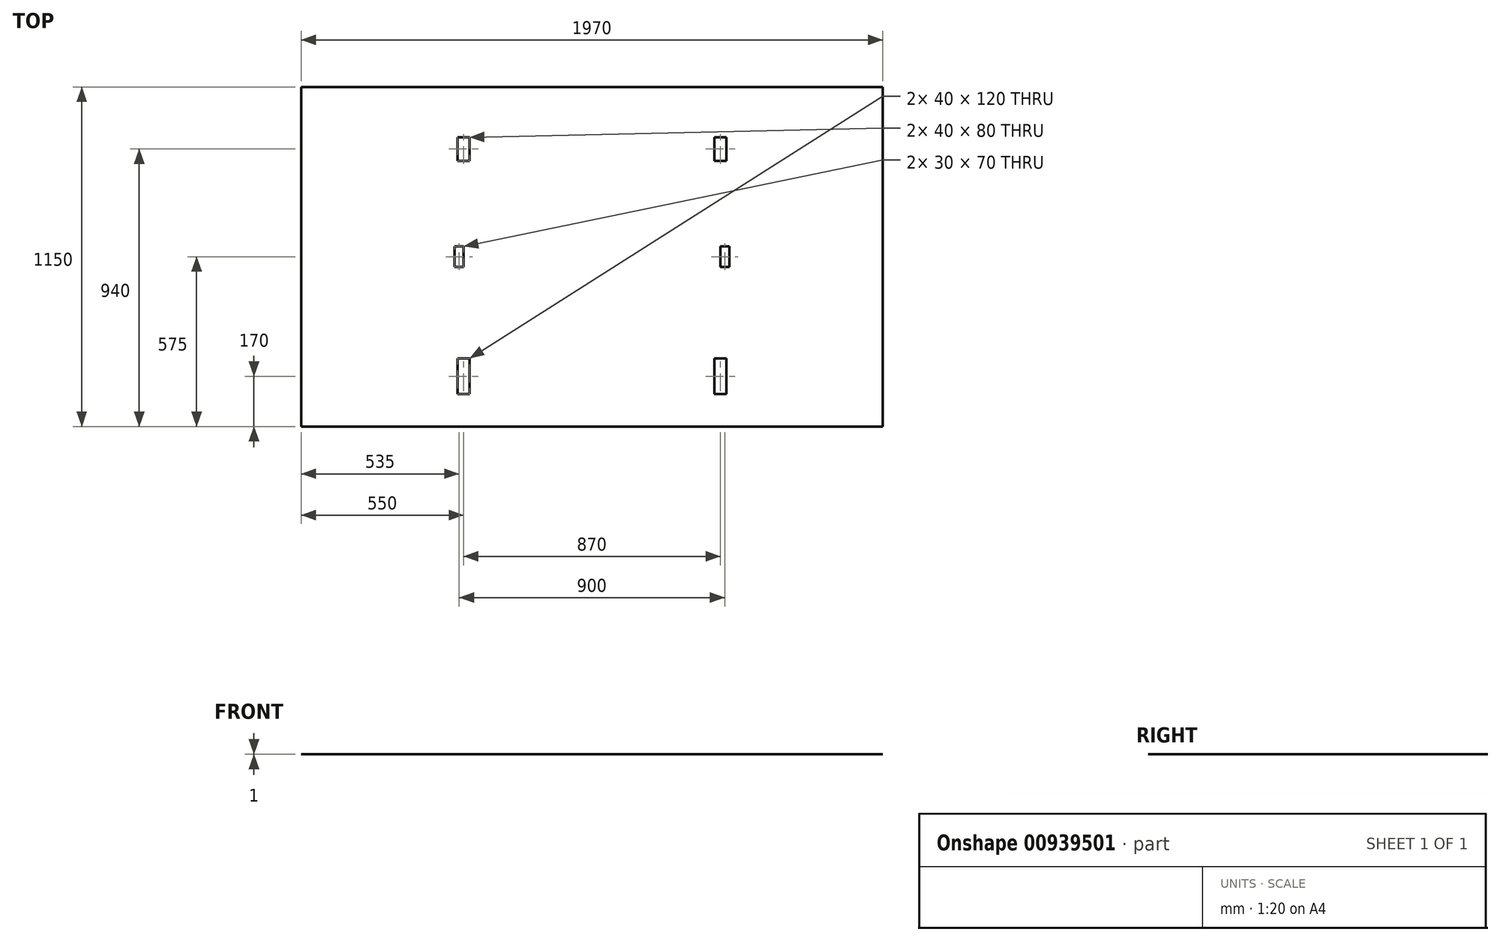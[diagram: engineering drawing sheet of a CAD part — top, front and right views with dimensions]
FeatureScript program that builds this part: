
annotation { "Feature Type Name" : "Feature", "Feature Type Description" : "" }
export const myFeature = defineFeature(function(context is Context, id is Id, definition is map)
    precondition{}
    {
        {
            var Q0;
            Q0=qCreatedBy(makeId("Top.planeOp"),FACE);
            var sketch = newSketch(context, id + "F0", { "sketchPlane" : qUnion([Q0])});
            skLineSegment(sketch, "E0.bottom", {"start": v(0, 0) * mm, "end": v(1970, 0) * mm});
            skLineSegment(sketch, "E0.top", {"start": v(0, 1150) * mm, "end": v(1970, 1150) * mm});
            skLineSegment(sketch, "E0.left", {"start": v(0, 0) * mm, "end": v(0, 1150) * mm});
            skLineSegment(sketch, "E0.right", {"start": v(1970, 0) * mm, "end": v(1970, 1150) * mm});
            skLineSegment(sketch, "E1", {"start": v(550, 1150) * mm, "end": v(550, 0) * mm, "construction": true});
            skLineSegment(sketch, "E2", {"start": v(1420, 1150) * mm, "end": v(1420, 0) * mm, "construction": true});
            skLineSegment(sketch, "E3", {"start": v(550, 900) * mm, "end": v(530, 900) * mm});
            skLineSegment(sketch, "E4", {"start": v(530, 900) * mm, "end": v(530, 980) * mm});
            skLineSegment(sketch, "E5", {"start": v(530, 980) * mm, "end": v(550, 980) * mm});
            skLineSegment(sketch, "E6.MirrorCS", {"start": v(570, 980) * mm, "end": v(550, 980) * mm});
            skLineSegment(sketch, "E7.MirrorCS", {"start": v(570, 900) * mm, "end": v(570, 980) * mm});
            skLineSegment(sketch, "E8.MirrorCS", {"start": v(550, 900) * mm, "end": v(570, 900) * mm});
            skLineSegment(sketch, "E9.bottom", {"start": v(550, 610) * mm, "end": v(520, 610) * mm});
            skLineSegment(sketch, "E9.top", {"start": v(550, 540) * mm, "end": v(520, 540) * mm});
            skLineSegment(sketch, "E9.left", {"start": v(550, 610) * mm, "end": v(550, 540) * mm});
            skLineSegment(sketch, "E9.right", {"start": v(520, 610) * mm, "end": v(520, 540) * mm});
            skLineSegment(sketch, "E10", {"start": v(550, 110) * mm, "end": v(530, 110) * mm});
            skLineSegment(sketch, "E11", {"start": v(530, 110) * mm, "end": v(530, 230) * mm});
            skLineSegment(sketch, "E12", {"start": v(530, 230) * mm, "end": v(550, 230) * mm});
            skLineSegment(sketch, "E13.MirrorCS", {"start": v(570, 230) * mm, "end": v(550, 230) * mm});
            skLineSegment(sketch, "E14.MirrorCS", {"start": v(570, 110) * mm, "end": v(570, 230) * mm});
            skLineSegment(sketch, "E15.MirrorCS", {"start": v(550, 110) * mm, "end": v(570, 110) * mm});
            skLineSegment(sketch, "E16", {"start": v(570, 940) * mm, "end": v(530, 940) * mm, "construction": true});
            skLineSegment(sketch, "E17", {"start": v(530, 940) * mm, "end": v(295.04, 940) * mm, "construction": true});
            skLineSegment(sketch, "E18", {"start": v(550, 575) * mm, "end": v(520, 575) * mm, "construction": true});
            skLineSegment(sketch, "E19", {"start": v(520, 575) * mm, "end": v(305.42, 575) * mm, "construction": true});
            skLineSegment(sketch, "E20", {"start": v(570, 170) * mm, "end": v(530, 170) * mm, "construction": true});
            skLineSegment(sketch, "E21", {"start": v(530, 170) * mm, "end": v(296.54, 170) * mm, "construction": true});
            skLineSegment(sketch, "E22", {"start": v(985, 1150) * mm, "end": v(985, 0) * mm, "construction": true});
            skLineSegment(sketch, "E23.MirrorCS", {"start": v(1440, 900) * mm, "end": v(1440, 980) * mm});
            skLineSegment(sketch, "E24.MirrorCS", {"start": v(1400, 900) * mm, "end": v(1400, 980) * mm});
            skLineSegment(sketch, "E25.MirrorCS", {"start": v(1450, 610) * mm, "end": v(1450, 540) * mm});
            skLineSegment(sketch, "E26.MirrorCS", {"start": v(1420, 540) * mm, "end": v(1450, 540) * mm});
            skLineSegment(sketch, "E27.MirrorCS", {"start": v(1420, 610) * mm, "end": v(1450, 610) * mm});
            skLineSegment(sketch, "E28.MirrorCS", {"start": v(1440, 230) * mm, "end": v(1420, 230) * mm});
            skLineSegment(sketch, "E29.MirrorCS", {"start": v(1400, 230) * mm, "end": v(1420, 230) * mm});
            skLineSegment(sketch, "E30.MirrorCS", {"start": v(1400, 110) * mm, "end": v(1400, 230) * mm});
            skLineSegment(sketch, "E31.MirrorCS", {"start": v(1440, 110) * mm, "end": v(1440, 230) * mm});
            skLineSegment(sketch, "E32.MirrorCS", {"start": v(1420, 110) * mm, "end": v(1440, 110) * mm});
            skLineSegment(sketch, "E33.MirrorCS", {"start": v(1420, 110) * mm, "end": v(1400, 110) * mm});
            skLineSegment(sketch, "E34.MirrorCS", {"start": v(1440, 980) * mm, "end": v(1420, 980) * mm});
            skLineSegment(sketch, "E35.MirrorCS", {"start": v(1400, 980) * mm, "end": v(1420, 980) * mm});
            skLineSegment(sketch, "E36.MirrorCS", {"start": v(1420, 900) * mm, "end": v(1440, 900) * mm});
            skLineSegment(sketch, "E37.MirrorCS", {"start": v(1420, 900) * mm, "end": v(1400, 900) * mm});
            skLineSegment(sketch, "E38.MirrorCS", {"start": v(1420, 610) * mm, "end": v(1420, 540) * mm});
            skSolve(sketch);
        }
        {
            var Q0;
            Q0=makeQuery(id+"F0.imprint","IMPRINT",FACE,{"disambiguationData":[TD([[makeQuery(id+"F0.imprint","IMPRINT",EDGE,{"derivedFrom":sQuery(id+"F0.wireOp",EDGE,"E0.bottom")}),1.0]])]});
            extrude(context, id + "F1", {"entities" : qUnion([Q0]), "depth" : 1 * mm, "offsetDistance" : 25 * mm});
        }
    });
